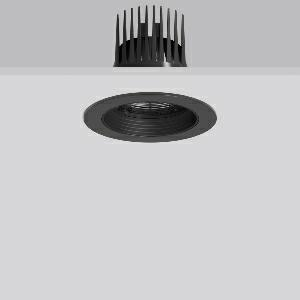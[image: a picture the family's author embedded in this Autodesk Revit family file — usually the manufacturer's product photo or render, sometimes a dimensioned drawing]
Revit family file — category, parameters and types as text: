
# Revit family: heledon_maxi_e_901767_003_3_56d9
name_source: partatom
category: Lighting Fixtures
units: mm (PartAtom-declared; Revit-internal decimal feet)

## family parameters
Cut with Voids When Loaded = No
Host = Face
Light Source = No
Part Type = Normal
Room Calculation Point = No
Round Connector Dimension = Use Diameter
Shared = No

## types (1)
- HELEDON maxi E (1 x LED Modul 935, 3750 lm, 3500)
    Apparent Load = 35 VA
    Approval mark = CE
    CIE Flux Codes = 97 100 100 100 100
    Color Rendering = 92
    Color Temperature = 3500
    Default Elevation = 1800 mm
    Description = Series: HELEDON maxi
Round recessed downlight. Housing: die-cast aluminium, powder-coated. Black plastic ring and recessed LED to prevent glare from the side. Optical assembly with lens made of plastic (polycarbonate) for the best homogeneous light distribution - can be changed without tools. Best colour rendering index Ra>90. Suitable for Recessed ceiling mounting. Installation without tools thanks to spring fastening system. Including separate LED converter with connecting cable 600 mm.High quality converter without flickering and stroboscopic effect. Through-wiring box (5 pole) available as accessory. The following accessories can be mounted without use of tools: interchangeable lenses, decorative glasses, honeycomb louvre, clear and frosted diffusers, white interchangeable plastic ring. 
Colour: deep black, matt (RAL 9005)
Diameter: 162 mm
Height: 3 mm
Cut-out diameter: 152 mm
Recess height: 200 mm
Luminaire: recess height: 135 mm
Lamp: LED
Socket: without socket
Colour temperature: 3500K
Colour rendering index (CRI): 92
System power: 35 W
Rated luminous flux: 3750 lm
Luminous efficiency: 107 lm/W
Control gear: Regulated power supply
Protection class: II
Type of protection: IP 20
    Height = 0 mm  [stored 0 ft]
    Lamp = 1 x LED Modul 935
    Lamp Light Flux = 3750 lm
    Lamp count = 1
    Length = 162 mm
    Lifetime = 50000 h
    Luminous efficacy = 107 lm/W
    Manufacturer = RZB
    ModVariant = No
    Model = 901767.003.3
    Mounting Place = Ceiling
    Mounting Type = Recessed
    Number of Poles = 1
    OnlyDefault = Yes
    Power Factor = 1
    Product Name = HELEDON maxi E
    Product group = Recessed downlights
    ProductGroupID = 402
    Protection Class = Protection class II
    Protection Degree = IP 20
    RLX_Detail_Level = 1
    RLX_Emergency_Light_Flux = 0 lm
    RLX_Emergency_Type = 0
    RLX_Emergency_Type_DB = No
    RlxData = <blob elided: 122221 chars, md5=4c2cdb40>
    Socket = socket
    Standby Power = 0 W
    System Light Flux = 3750 lm
    System Power = 35 W
    Type Comments = Product without accessories
    Type Image = 901663.003.jpg
    URL = http://relux.com
    VarID = ---
    Voltage = 230 V
    Voltage Range = 220-240 V
    Weight = 0.00 kg
    Width = 0 mm  [stored 0 ft]

note: [stored X ft] marks values corroborated as IEEE doubles in the binary element streams (Revit-internal decimal feet)

## geometry (parser evidence)
native form markers: Blend x4, Sweep x12
no freeform markers — native parametric forms only
